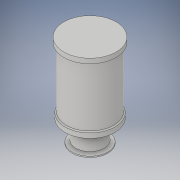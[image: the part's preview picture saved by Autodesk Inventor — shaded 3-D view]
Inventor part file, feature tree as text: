
AUTODESK INVENTOR PART (.ipt)
format: ipt  version: 2018 (Build 220112000, 112)  size: 138,752 bytes
history: native  units: in
note: dims shown in document units (in); Inventor stores cm internally (conversion verified against a paired STEP export)
features: revolve x1, sketch x1
ambient origin geometry x8: Origin, YZ Plane, XZ Plane, XY Plane, X Axis, Y Axis, Z Axis, Center Point
bodies: Solid1 (feature_tree)
feature tree (2):
  revolve  "Revolution1"  [1 undecoded]
  sketch  "Sketch1"  dims[d1=5.0in d2=1.0in d3=0.5in d4=3.75in d5=0.25in d6=22.0in d7=0.25in d9=2.5in d10=3.0in d11=4.0in d12=0.2405in d13=135.0deg d14=1.0in d15=0.125in d16=90.0deg]
note: 1 required parameter value undecoded (feature->parameter linkage not recoverable at this tier; creation-order binding heuristic only, values carry confidence <= 0.55)
